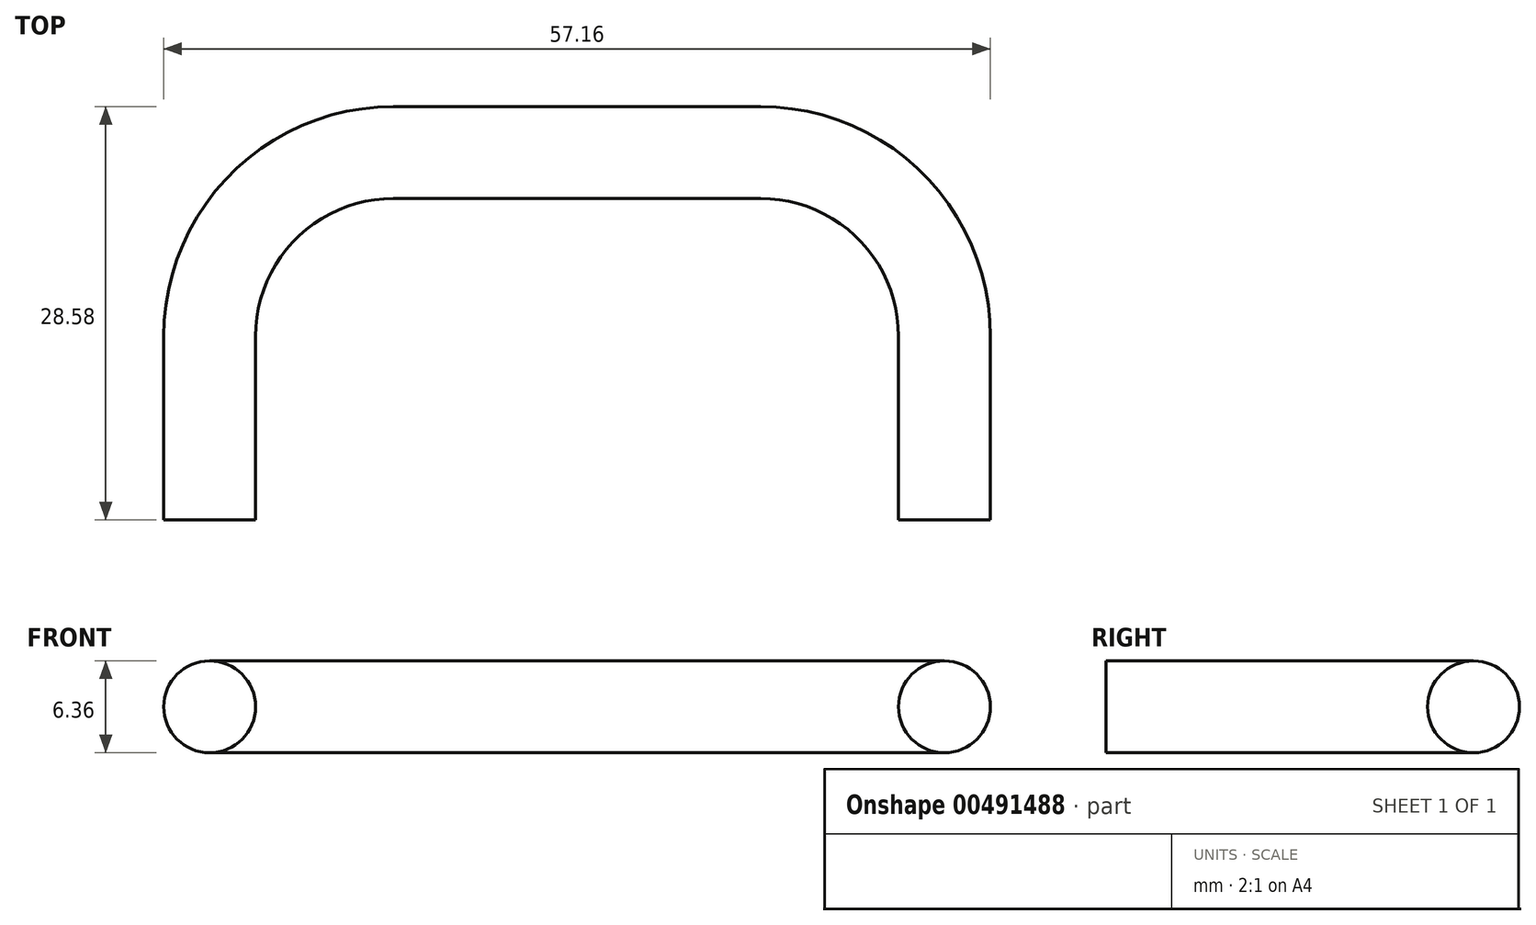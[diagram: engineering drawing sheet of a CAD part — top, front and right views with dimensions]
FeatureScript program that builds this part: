
annotation { "Feature Type Name" : "Feature", "Feature Type Description" : "" }
export const myFeature = defineFeature(function(context is Context, id is Id, definition is map)
    precondition{}
    {
        {
            var Q0;
            Q0=qCreatedBy(makeId("Top.planeOp"),FACE);
            var sketch = newSketch(context, id + "F0", { "sketchPlane" : qUnion([Q0])});
            skPoint(sketch, "E0.middle", {"position": v(0, 0) * mm});
            skPoint(sketch, "E1", {"position": v(12.7, 25.4) * mm});
            skPoint(sketch, "E2", {"position": v(-12.7, 25.4) * mm});
            skPoint(sketch, "E3", {"position": v(-25.4, 12.7) * mm});
            skPoint(sketch, "E4", {"position": v(25.4, 12.7) * mm});
            skArc(sketch, "E5", {"start": v(-25.4, 12.7) * mm, "mid": v(-21.68, 21.68) * mm, "end": v(-12.7, 25.4) * mm});
            skArc(sketch, "E6", {"start": v(25.4, 12.7) * mm, "mid": v(21.68, 21.68) * mm, "end": v(12.7, 25.4) * mm});
            skLineSegment(sketch, "E7", {"start": v(-12.7, 25.4) * mm, "end": v(12.7, 25.4) * mm});
            skLineSegment(sketch, "E8", {"start": v(-25.4, 12.7) * mm, "end": v(-25.4, 0) * mm});
            skLineSegment(sketch, "E9", {"start": v(25.4, 12.7) * mm, "end": v(25.4, 0) * mm});
            skSolve(sketch);
        }
        {
            var Q0;
            Q0=qCreatedBy(makeId("Front.planeOp"),FACE);
            var sketch = newSketch(context, id + "F1", { "sketchPlane" : qUnion([Q0])});
            skPoint(sketch, "E10", {"position": v(25.4, 0) * mm});
            skCircle(sketch, "E11", {"center": v(25.4, 0) * mm, "radius": 3.18 * mm});
            skSolve(sketch);
        }
        {
            var Q0;
            Q0=makeQuery(id+"F1.imprint","IMPRINT",FACE,{"disambiguationData":[TD([[makeQuery(id+"F1.imprint","IMPRINT",EDGE,{"derivedFrom":sQuery(id+"F1.wireOp",EDGE,"E11")}),1.0]])]});
            var Q1;
            Q1=sQuery(id+"F0.wireOp",EDGE,"E9");
            var Q2;
            Q2=sQuery(id+"F0.wireOp",EDGE,"E6");
            var Q3;
            Q3=sQuery(id+"F0.wireOp",EDGE,"E7");
            var Q4;
            Q4=sQuery(id+"F0.wireOp",EDGE,"E5");
            var Q5;
            Q5=sQuery(id+"F0.wireOp",EDGE,"E8");
            sweep(context, id + "F2", {"profiles" : qUnion([Q0]), "path" : qUnion([Q1, Q2, Q3, Q4, Q5])});
        }
    });
